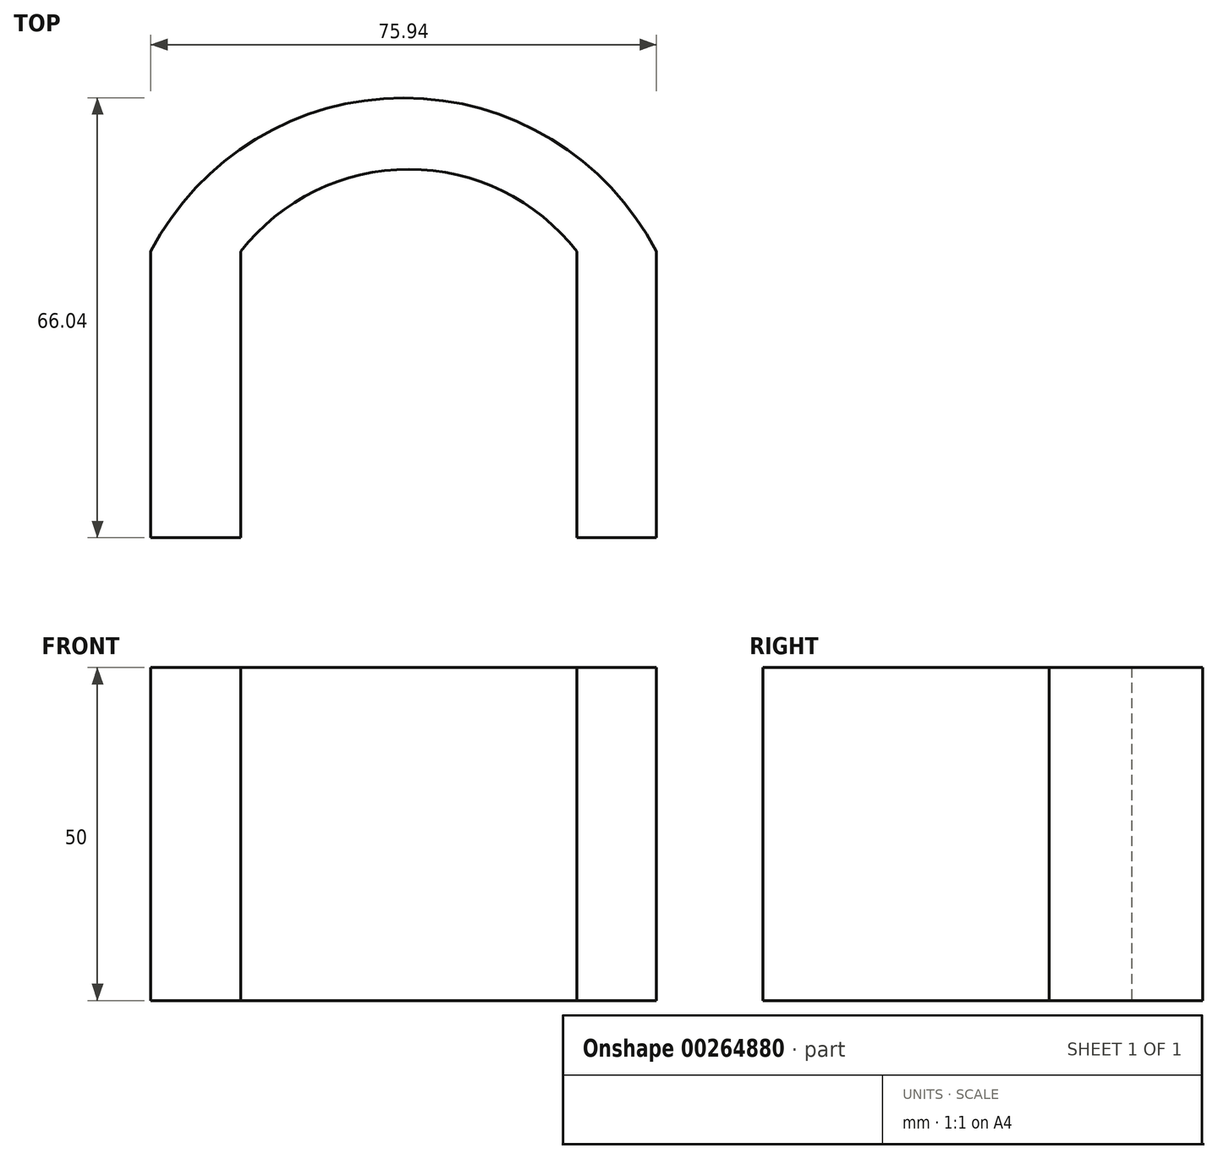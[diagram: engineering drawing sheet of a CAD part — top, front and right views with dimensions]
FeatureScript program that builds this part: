
annotation { "Feature Type Name" : "Feature", "Feature Type Description" : "" }
export const myFeature = defineFeature(function(context is Context, id is Id, definition is map)
    precondition{}
    {
        {
            var Q0;
            Q0=qCreatedBy(makeId("Top.planeOp"),FACE);
            var sketch = newSketch(context, id + "F0", { "sketchPlane" : qUnion([Q0])});
            skLineSegment(sketch, "E0", {"start": v(-33.42, 0) * mm, "end": v(42.52, 0) * mm});
            skLineSegment(sketch, "E1", {"start": v(42.52, 0) * mm, "end": v(42.52, 42.99) * mm});
            skLineSegment(sketch, "E2", {"start": v(-33.42, 0) * mm, "end": v(-33.42, 42.99) * mm});
            skArc(sketch, "E3", {"start": v(42.52, 42.99) * mm, "mid": v(4.55, 66.04) * mm, "end": v(-33.42, 42.99) * mm});
            skLineSegment(sketch, "E4", {"start": v(-19.92, 0) * mm, "end": v(-19.92, 42.99) * mm});
            skLineSegment(sketch, "E5", {"start": v(30.6, 0) * mm, "end": v(30.6, 42.99) * mm});
            skArc(sketch, "E6", {"start": v(30.6, 42.99) * mm, "mid": v(5.33, 55.33) * mm, "end": v(-19.92, 42.99) * mm});
            skSolve(sketch);
        }
        {
            var Q0;
            Q0 = qSketchRegion(id + "F0", true);
            extrude(context, id + "F1", {"entities" : qUnion([Q0]), "depth" : 50 * mm});
        }
        {
            var Q0;
            {var subQ0=sQuery(id+"F0.wireOp",EDGE,"E4");Q0=makeQuery(id+"F0.imprint","IMPRINT",FACE,{"disambiguationData":[TD([[makeQuery(id+"F0.imprint","IMPRINT",EDGE,{"derivedFrom":subQ0}),-1.0]])]});}
            extrude(context, id + "F2", {"entities" : qUnion([Q0]), "operationType" : NewBodyOperationType.REMOVE, "endBound" : BoundingType.THROUGH_ALL, "depth" : 25.4 * mm});
        }
    });
